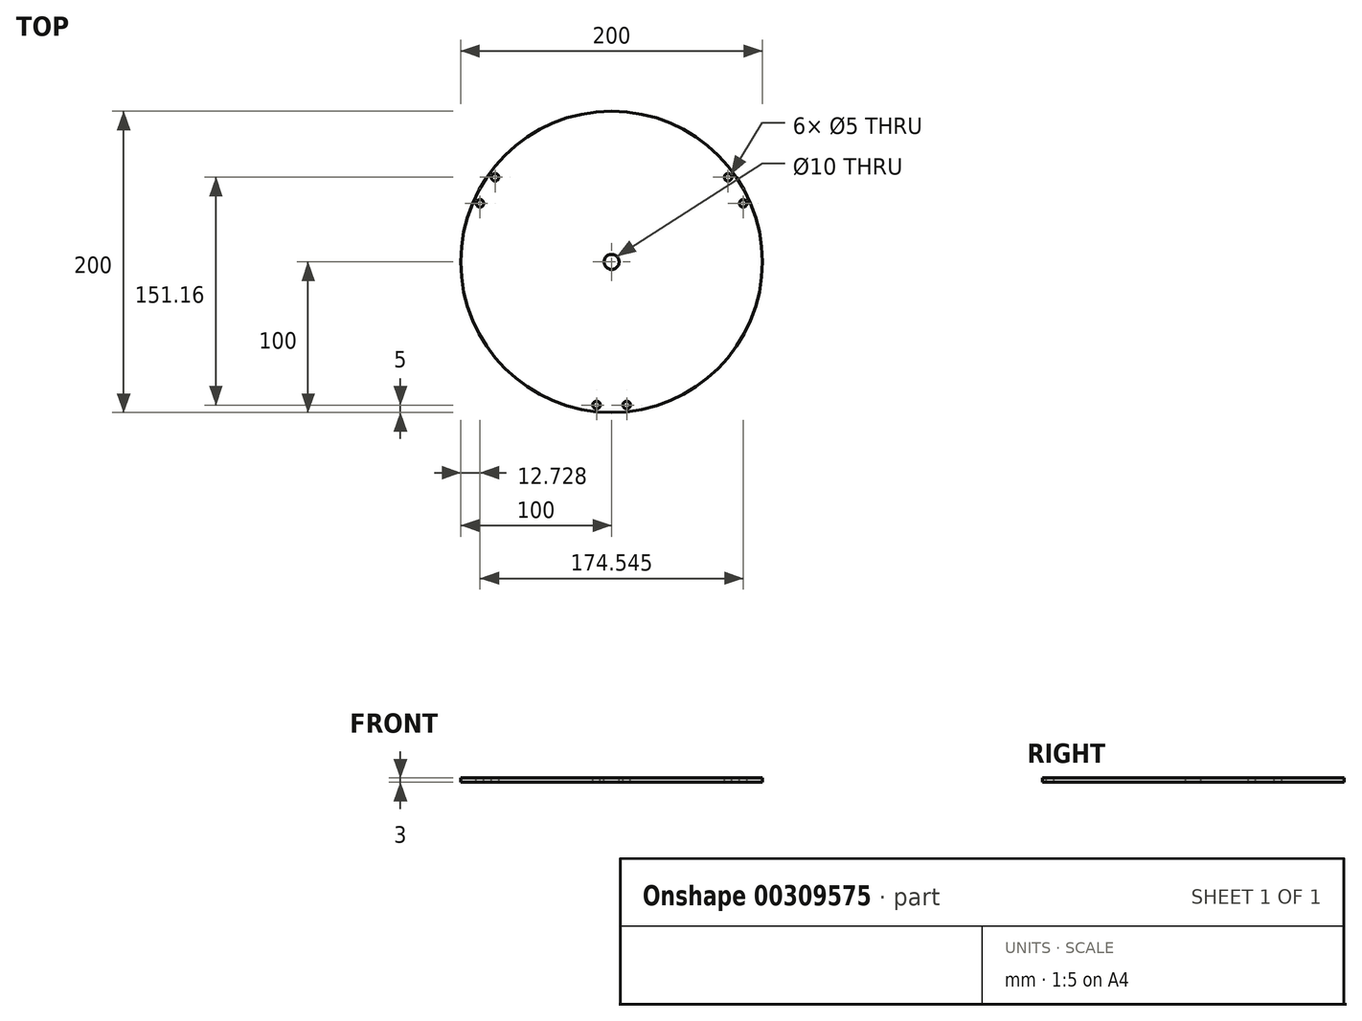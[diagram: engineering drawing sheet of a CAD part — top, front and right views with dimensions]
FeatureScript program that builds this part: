
annotation { "Feature Type Name" : "Feature", "Feature Type Description" : "" }
export const myFeature = defineFeature(function(context is Context, id is Id, definition is map)
    precondition{}
    {
        {
            var Q0;
            Q0=qCreatedBy(makeId("Top.planeOp"),FACE);
            var sketch = newSketch(context, id + "F0", { "sketchPlane" : qUnion([Q0])});
            skCircle(sketch, "E0", {"center": v(0, 0) * mm, "radius": 100 * mm});
            skSolve(sketch);
        }
        {
            var Q0;
            Q0 = qSketchRegion(id + "F0", true);
            extrude(context, id + "F1", {"entities" : qUnion([Q0]), "depth" : 3 * mm, "offsetDistance" : 25 * mm});
        }
        {
            var Q0;
            Q0=makeQuery(id+"F1.opExtrude","CAP_FACE",FACE,{"disambiguationData":[OSD([sQuery(id+"F0.wireOp",EDGE,"E0")])],"isStart":false});
            var sketch = newSketch(context, id + "F2", { "sketchPlane" : qUnion([Q0])});
            skPoint(sketch, "E1", {"position": v(0, 0) * mm});
            skPoint(sketch, "E2", {"position": v(-10, -95) * mm});
            skPoint(sketch, "E3", {"position": v(10, -95) * mm});
            skLineSegment(sketch, "E4", {"start": v(0, 0) * mm, "end": v(0, -99.62) * mm, "construction": true});
            skPoint(sketch, "E5.1.0", {"position": v(77.27, 56.16) * mm});
            skPoint(sketch, "E5.1.1", {"position": v(87.27, 38.84) * mm});
            skPoint(sketch, "E5.2.0", {"position": v(-87.27, 38.84) * mm});
            skPoint(sketch, "E5.2.1", {"position": v(-77.27, 56.16) * mm});
            skSolve(sketch);
        }
        {
            var Q0;
            Q0=sQuery(id+"F2.wireOp",VERTEX,"E1");
            var Q1;
            Q1=makeQuery(id+"F1.opExtrude","SWEPT_BODY",BODY,{"disambiguationData":[OSD([sQuery(id+"F0.wireOp",EDGE,"E0")])]});
            hole(context, id + "F3", {"style" : HoleStyle.SIMPLE, "endStyle" : HoleEndStyle.THROUGH, "holeDiameter" : 10 * mm, "majorDiameter" : 5 * mm, "isTappedThrough" : true, "tappedDepth" : 12 * mm, "tapClearance" : 3, "startFromSketch" : true, "locations" : qUnion([Q0]), "scope" : qUnion([Q1])});
        }
        {
            var Q0;
            Q0=sQuery(id+"F2.wireOp",VERTEX,"E2");
            var Q1;
            Q1=sQuery(id+"F2.wireOp",VERTEX,"E3");
            var Q2;
            Q2=sQuery(id+"F2.wireOp",VERTEX,"E5.1.1");
            var Q3;
            Q3=sQuery(id+"F2.wireOp",VERTEX,"E5.1.0");
            var Q4;
            Q4=sQuery(id+"F2.wireOp",VERTEX,"E5.2.1");
            var Q5;
            Q5=sQuery(id+"F2.wireOp",VERTEX,"E5.2.0");
            var Q6;
            Q6=makeQuery(id+"F1.opExtrude","SWEPT_BODY",BODY,{"disambiguationData":[OSD([sQuery(id+"F0.wireOp",EDGE,"E0")])]});
            hole(context, id + "F4", {"style" : HoleStyle.SIMPLE, "endStyle" : HoleEndStyle.THROUGH, "holeDiameter" : 5 * mm, "majorDiameter" : 5 * mm, "isTappedThrough" : true, "tappedDepth" : 12 * mm, "tapClearance" : 3, "startFromSketch" : true, "locations" : qUnion([Q0, Q1, Q2, Q3, Q4, Q5]), "scope" : qUnion([Q6])});
        }
    });
